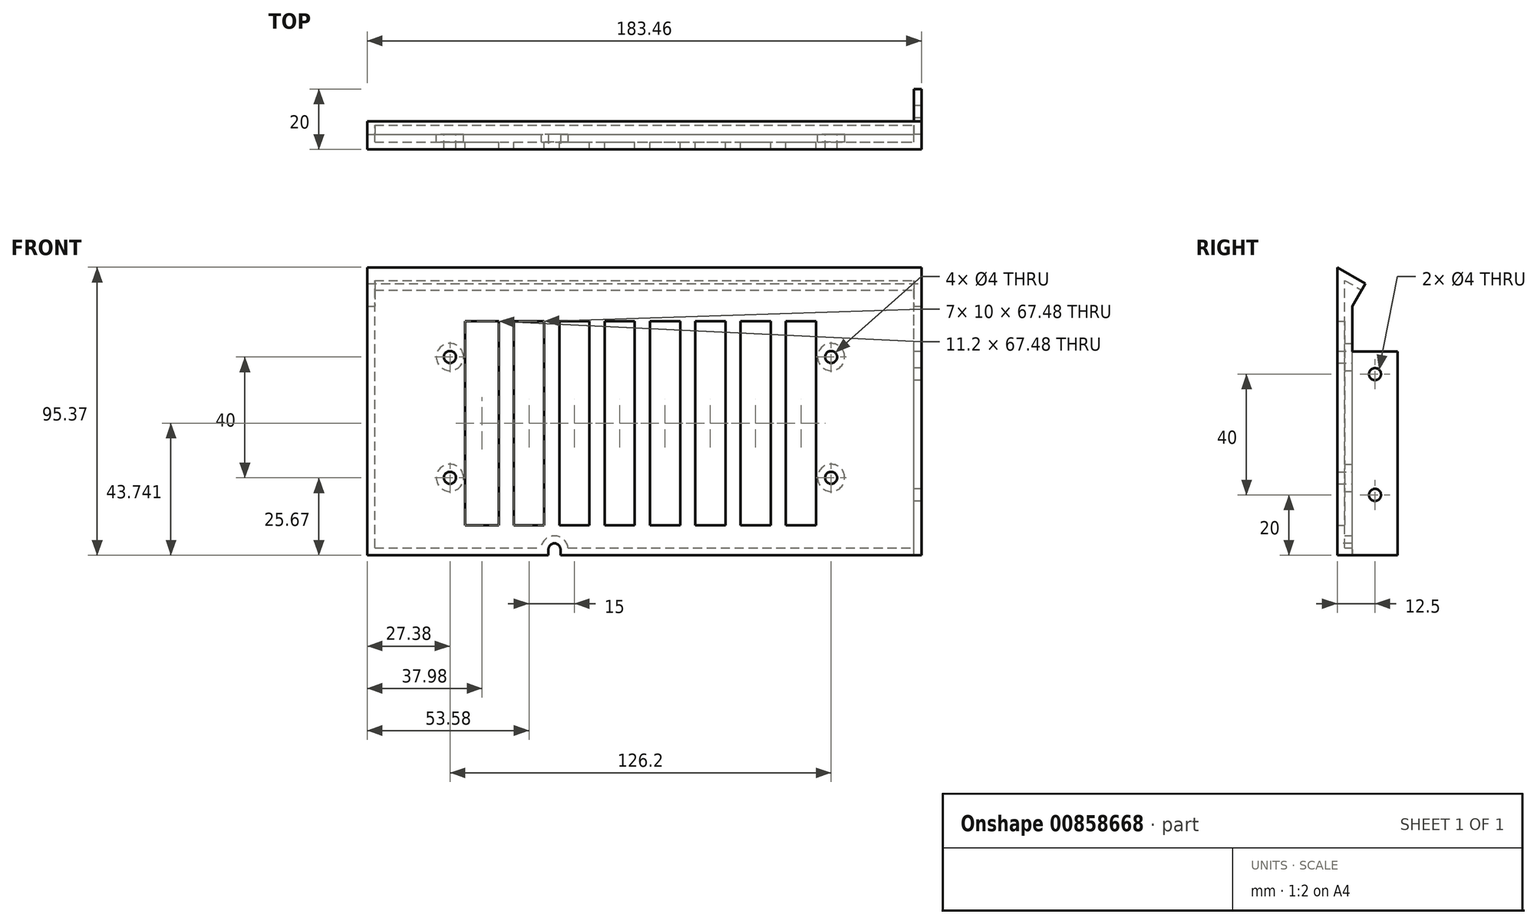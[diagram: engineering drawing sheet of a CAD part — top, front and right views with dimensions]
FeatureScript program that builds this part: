
annotation { "Feature Type Name" : "Feature", "Feature Type Description" : "" }
export const myFeature = defineFeature(function(context is Context, id is Id, definition is map)
    precondition{}
    {
        {
            var Q0;
            Q0=qCreatedBy(makeId("Front.planeOp"),FACE);
            var sketch = newSketch(context, id + "F0", { "sketchPlane" : qUnion([Q0])});
            skLineSegment(sketch, "E0.bottom", {"start": v(0, 0) * mm, "end": v(180.96, 0) * mm});
            skLineSegment(sketch, "E0.top", {"start": v(0, 95.37) * mm, "end": v(180.96, 95.37) * mm});
            skLineSegment(sketch, "E0.left", {"start": v(0, 0) * mm, "end": v(0, 95.37) * mm});
            skLineSegment(sketch, "E0.right", {"start": v(180.96, 0) * mm, "end": v(180.96, 95.37) * mm});
            skCircle(sketch, "E1", {"center": v(27.38, 65.67) * mm, "radius": 2 * mm});
            skCircle(sketch, "E2", {"center": v(153.58, 65.67) * mm, "radius": 2 * mm});
            skCircle(sketch, "E3", {"center": v(27.38, 25.67) * mm, "radius": 2 * mm});
            skCircle(sketch, "E4", {"center": v(153.58, 25.67) * mm, "radius": 2 * mm});
            skLineSegment(sketch, "E5", {"start": v(90.48, 95.37) * mm, "end": v(90.48, 0) * mm, "construction": true});
            skSolve(sketch);
        }
        {
            var Q0;
            Q0 = qSketchRegion(id + "F0", true);
            extrude(context, id + "F1", {"entities" : qUnion([Q0]), "depth" : 5 * mm, "offsetDistance" : 25 * mm});
        }
        {
            var Q0;
            Q0=makeQuery(id+"F1.opExtrude","SWEPT_FACE",FACE,{"disambiguationData":[OSD([sQuery(id+"F0.wireOp",EDGE,"E0.left")])]});
            var sketch = newSketch(context, id + "F2", { "sketchPlane" : qUnion([Q0])});
            skLineSegment(sketch, "E6", {"start": v(5, 95.37) * mm, "end": v(0, 92.48) * mm});
            skLineSegment(sketch, "E7", {"start": v(5, 95.37) * mm, "end": v(0, 95.37) * mm});
            skLineSegment(sketch, "E8", {"start": v(0, 95.37) * mm, "end": v(0, 92.48) * mm});
            skSolve(sketch);
        }
        {
            var Q0;
            Q0 = qSketchRegion(id + "F2", true);
            extrude(context, id + "F3", {"entities" : qUnion([Q0]), "operationType" : NewBodyOperationType.REMOVE, "endBound" : BoundingType.THROUGH_ALL, "oppositeDirection" : true, "depth" : 25 * mm, "offsetDistance" : 25 * mm});
        }
        {
            var Q0;
            Q0=makeQuery(id+"F1.opExtrude","SWEPT_FACE",FACE,{"disambiguationData":[OSD([sQuery(id+"F0.wireOp",EDGE,"E0.right")])]});
            var sketch = newSketch(context, id + "F4", { "sketchPlane" : qUnion([Q0])});
            skLineSegment(sketch, "E9", {"start": v(0, 92.48) * mm, "end": v(4.33, 89.98) * mm});
            skLineSegment(sketch, "E10", {"start": v(4.33, 89.98) * mm, "end": v(0, 82.48) * mm});
            skLineSegment(sketch, "E11", {"start": v(0, 82.48) * mm, "end": v(0, 92.48) * mm});
            skSolve(sketch);
        }
        {
            var Q0;
            Q0 = qSketchRegion(id + "F4", true);
            var Q1;
            Q1=makeQuery(id+"F1.opExtrude","SWEPT_FACE",FACE,{"disambiguationData":[OSD([sQuery(id+"F0.wireOp",EDGE,"E0.left")])]});
            extrude(context, id + "F5", {"entities" : qUnion([Q0]), "operationType" : NewBodyOperationType.ADD, "endBound" : BoundingType.UP_TO_SURFACE, "oppositeDirection" : true, "depth" : 25 * mm, "endBoundEntityFace" : qUnion([Q1]), "offsetDistance" : 25 * mm});
        }
        {
            var Q0;
            Q0=makeQuery(id+"F1.opExtrude","CAP_FACE",FACE,{"disambiguationData":[OSD([sQuery(id+"F0.wireOp",EDGE,"E0.bottom"),sQuery(id+"F0.wireOp",EDGE,"E0.top"),sQuery(id+"F0.wireOp",EDGE,"E0.left"),sQuery(id+"F0.wireOp",EDGE,"E0.right"),sQuery(id+"F0.wireOp",EDGE,"E1"),sQuery(id+"F0.wireOp",EDGE,"E2"),sQuery(id+"F0.wireOp",EDGE,"E3"),sQuery(id+"F0.wireOp",EDGE,"E4")])],"isStart":false});
            var sketch = newSketch(context, id + "F6", { "sketchPlane" : qUnion([Q0])});
            skArc(sketch, "E12", {"start": v(60, 1.98) * mm, "mid": v(61.98, 3.97) * mm, "end": v(63.97, 1.98) * mm});
            skLineSegment(sketch, "E13", {"start": v(60, 0) * mm, "end": v(60, 1.98) * mm});
            skLineSegment(sketch, "E14", {"start": v(63.97, 1.98) * mm, "end": v(63.97, 0) * mm});
            skLineSegment(sketch, "E15", {"start": v(60, 0) * mm, "end": v(63.97, 0) * mm});
            skSolve(sketch);
        }
        {
            var Q0;
            Q0 = qSketchRegion(id + "F6", true);
            extrude(context, id + "F7", {"entities" : qUnion([Q0]), "operationType" : NewBodyOperationType.REMOVE, "endBound" : BoundingType.THROUGH_ALL, "oppositeDirection" : true, "depth" : 25 * mm, "offsetDistance" : 25 * mm});
        }
        {
            var Q0;
            Q0=makeQuery(id+"F5.boolean.opBoolean","MERGE",FACE,{"derivedFrom":[makeQuery(id+"F1.opExtrude","SWEPT_FACE",FACE,{"disambiguationData":[OSD([sQuery(id+"F0.wireOp",EDGE,"E0.right")])]}),makeQuery(id+"F5.opExtrude","CAP_FACE",FACE,{"disambiguationData":[OSD([sQuery(id+"F4.wireOp",EDGE,"E9"),sQuery(id+"F4.wireOp",EDGE,"E10"),sQuery(id+"F4.wireOp",EDGE,"E11")])],"isStart":true})]});
            var sketch = newSketch(context, id + "F8", { "sketchPlane" : qUnion([Q0])});
            skLineSegment(sketch, "E16.bottom", {"start": v(-5, 0) * mm, "end": v(15, 0) * mm});
            skLineSegment(sketch, "E16.top", {"start": v(-5, 67.5) * mm, "end": v(15, 67.5) * mm});
            skLineSegment(sketch, "E16.left", {"start": v(-5, 0) * mm, "end": v(-5, 67.5) * mm});
            skLineSegment(sketch, "E16.right", {"start": v(15, 0) * mm, "end": v(15, 67.5) * mm});
            skCircle(sketch, "E17", {"center": v(7.5, 20) * mm, "radius": 2 * mm});
            skCircle(sketch, "E18", {"center": v(7.5, 60) * mm, "radius": 2 * mm});
            skLineSegment(sketch, "E19", {"start": v(-5, 67.5) * mm, "end": v(-5, 95.37) * mm});
            skLineSegment(sketch, "E20", {"start": v(-5, 95.37) * mm, "end": v(4.33, 89.98) * mm});
            skLineSegment(sketch, "E21", {"start": v(4.33, 89.98) * mm, "end": v(0, 82.48) * mm});
            skLineSegment(sketch, "E22", {"start": v(0, 82.48) * mm, "end": v(0, 67.5) * mm});
            skLineSegment(sketch, "E23", {"start": v(0, 67.5) * mm, "end": v(-5, 67.5) * mm});
            skSolve(sketch);
        }
        {
            var Q0;
            Q0 = qSketchRegion(id + "F8", true);
            extrude(context, id + "F9", {"entities" : qUnion([Q0]), "operationType" : NewBodyOperationType.ADD, "depth" : 2.5 * mm, "offsetDistance" : 25 * mm});
        }
        {
            var Q0;
            Q0=makeQuery(id+"F9.boolean.opBoolean","MERGE",FACE,{"derivedFrom":[makeQuery(id+"F1.opExtrude","CAP_FACE",FACE,{"disambiguationData":[OSD([sQuery(id+"F0.wireOp",EDGE,"E0.bottom"),sQuery(id+"F0.wireOp",EDGE,"E0.top"),sQuery(id+"F0.wireOp",EDGE,"E0.left"),sQuery(id+"F0.wireOp",EDGE,"E0.right"),sQuery(id+"F0.wireOp",EDGE,"E1"),sQuery(id+"F0.wireOp",EDGE,"E2"),sQuery(id+"F0.wireOp",EDGE,"E3"),sQuery(id+"F0.wireOp",EDGE,"E4")])],"isStart":true}),makeQuery(id+"F9.opExtrude","SWEPT_FACE",FACE,{"disambiguationData":[OSD([sQuery(id+"F8.wireOp",EDGE,"E22")])]})]});
            var Q1;
            Q1=makeQuery(id+"F9.boolean.opBoolean","MERGE",FACE,{"derivedFrom":[makeQuery(id+"F5.opExtrude","SWEPT_FACE",FACE,{"disambiguationData":[OSD([sQuery(id+"F4.wireOp",EDGE,"E10")])]}),makeQuery(id+"F9.opExtrude","SWEPT_FACE",FACE,{"disambiguationData":[OSD([sQuery(id+"F8.wireOp",EDGE,"E21")])]})]});
            shell(context, id + "F10", {"entities" : qUnion([Q0, Q1]), "thickness" : 2.5 * mm});
        }
        {
            var Q0;
            Q0=makeQuery(id+"F1.opExtrude","CAP_FACE",FACE,{"disambiguationData":[OSD([sQuery(id+"F0.wireOp",EDGE,"E0.bottom"),sQuery(id+"F0.wireOp",EDGE,"E0.top"),sQuery(id+"F0.wireOp",EDGE,"E0.left"),sQuery(id+"F0.wireOp",EDGE,"E0.right"),sQuery(id+"F0.wireOp",EDGE,"E1"),sQuery(id+"F0.wireOp",EDGE,"E2"),sQuery(id+"F0.wireOp",EDGE,"E3"),sQuery(id+"F0.wireOp",EDGE,"E4")])],"isStart":true});
            var sketch = newSketch(context, id + "F11", { "sketchPlane" : qUnion([Q0])});
            skLineSegment(sketch, "E24.bottom", {"start": v(-148.58, 77.48) * mm, "end": v(-32.38, 77.48) * mm, "construction": true});
            skLineSegment(sketch, "E24.top", {"start": v(-148.58, 10) * mm, "end": v(-32.38, 10) * mm, "construction": true});
            skLineSegment(sketch, "E24.left", {"start": v(-148.58, 77.48) * mm, "end": v(-148.58, 10) * mm});
            skLineSegment(sketch, "E24.right", {"start": v(-32.38, 77.48) * mm, "end": v(-32.38, 10) * mm});
            skPoint(sketch, "E25", {"position": v(-153.58, 65.67) * mm});
            skPoint(sketch, "E26", {"position": v(-27.38, 65.67) * mm});
            skLineSegment(sketch, "E27", {"start": v(-138.58, 77.48) * mm, "end": v(-138.58, 10) * mm});
            skLineSegment(sketch, "E28", {"start": v(-148.58, 77.48) * mm, "end": v(-138.58, 77.48) * mm});
            skLineSegment(sketch, "E29", {"start": v(-138.58, 10) * mm, "end": v(-148.58, 10) * mm});
            skLineSegment(sketch, "E30.bottom", {"start": v(-133.58, 10) * mm, "end": v(-123.58, 10) * mm});
            skLineSegment(sketch, "E30.top", {"start": v(-133.58, 77.48) * mm, "end": v(-123.58, 77.48) * mm});
            skLineSegment(sketch, "E30.left", {"start": v(-133.58, 10) * mm, "end": v(-133.58, 77.48) * mm});
            skLineSegment(sketch, "E30.right", {"start": v(-123.58, 10) * mm, "end": v(-123.58, 77.48) * mm});
            skLineSegment(sketch, "E31.bottom", {"start": v(-118.58, 10) * mm, "end": v(-108.58, 10) * mm});
            skLineSegment(sketch, "E31.top", {"start": v(-118.58, 77.48) * mm, "end": v(-108.58, 77.48) * mm});
            skLineSegment(sketch, "E31.left", {"start": v(-118.58, 10) * mm, "end": v(-118.58, 77.48) * mm});
            skLineSegment(sketch, "E31.right", {"start": v(-108.58, 10) * mm, "end": v(-108.58, 77.48) * mm});
            skLineSegment(sketch, "E32.bottom", {"start": v(-103.58, 10) * mm, "end": v(-93.58, 10) * mm});
            skLineSegment(sketch, "E32.top", {"start": v(-103.58, 77.48) * mm, "end": v(-93.58, 77.48) * mm});
            skLineSegment(sketch, "E32.left", {"start": v(-103.58, 10) * mm, "end": v(-103.58, 77.48) * mm});
            skLineSegment(sketch, "E32.right", {"start": v(-93.58, 10) * mm, "end": v(-93.58, 77.48) * mm});
            skLineSegment(sketch, "E33.bottom", {"start": v(-88.58, 10) * mm, "end": v(-78.58, 10) * mm});
            skLineSegment(sketch, "E33.top", {"start": v(-88.58, 77.48) * mm, "end": v(-78.58, 77.48) * mm});
            skLineSegment(sketch, "E33.left", {"start": v(-88.58, 10) * mm, "end": v(-88.58, 77.48) * mm});
            skLineSegment(sketch, "E33.right", {"start": v(-78.58, 10) * mm, "end": v(-78.58, 77.48) * mm});
            skLineSegment(sketch, "E34.bottom", {"start": v(-73.58, 10) * mm, "end": v(-63.58, 10) * mm});
            skLineSegment(sketch, "E34.top", {"start": v(-73.58, 77.48) * mm, "end": v(-63.58, 77.48) * mm});
            skLineSegment(sketch, "E34.left", {"start": v(-73.58, 10) * mm, "end": v(-73.58, 77.48) * mm});
            skLineSegment(sketch, "E34.right", {"start": v(-63.58, 10) * mm, "end": v(-63.58, 77.48) * mm});
            skLineSegment(sketch, "E35.bottom", {"start": v(-58.58, 10) * mm, "end": v(-48.58, 10) * mm});
            skLineSegment(sketch, "E35.top", {"start": v(-58.58, 77.48) * mm, "end": v(-48.58, 77.48) * mm});
            skLineSegment(sketch, "E35.left", {"start": v(-58.58, 10) * mm, "end": v(-58.58, 77.48) * mm});
            skLineSegment(sketch, "E35.right", {"start": v(-48.58, 10) * mm, "end": v(-48.58, 77.48) * mm});
            skLineSegment(sketch, "E36", {"start": v(-32.38, 77.48) * mm, "end": v(-43.58, 77.48) * mm});
            skLineSegment(sketch, "E37", {"start": v(-43.58, 77.48) * mm, "end": v(-43.58, 10) * mm});
            skLineSegment(sketch, "E38", {"start": v(-43.58, 10) * mm, "end": v(-32.38, 10) * mm});
            skSolve(sketch);
        }
        {
            var Q0;
            Q0 = qSketchRegion(id + "F11", true);
            extrude(context, id + "F12", {"entities" : qUnion([Q0]), "operationType" : NewBodyOperationType.REMOVE, "endBound" : BoundingType.THROUGH_ALL, "oppositeDirection" : true, "depth" : 25 * mm, "offsetDistance" : 25 * mm});
        }
    });
